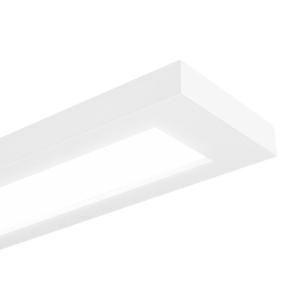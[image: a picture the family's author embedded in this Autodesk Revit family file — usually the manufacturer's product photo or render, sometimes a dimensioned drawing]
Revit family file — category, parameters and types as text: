
# Revit family: 3f_filippi_-_3f_travetta_op_3f_filippi_-_10731_-_3f_travetta_led_1x18w_op_l1290
name_source: partatom
category: Lighting Fixtures
units: mm (PartAtom-declared; Revit-internal decimal feet)

## family parameters
Cut with Voids When Loaded = No
Host = Face
Light Source = No
Part Type = Normal
Room Calculation Point = No
Round Connector Dimension = Use Diameter
Shared = No

## types (1)
- 3F Filippi - 3F Travetta OP (1 x LED, 2265 lm, 20 W, 4000 K)
    Apparent Load = 20 VA
    Approval mark = ENEC
    CIE Flux Codes = 49 81 97 100 100
    Color Rendering = 80
    Color Temperature = 4000 K
    Control Gear = Electronic ballast
    Default Elevation = 1800 mm
    Description = ILLUMINOTECHNICAL
Luminous efficiency 100% (DLOR 100%, ULOR 0%).
Initial luminous flux of the luminaire 2265 lm.
Direct symmetric distribution.
Installation Interdistance Transv.D = 1.20 x hu - Long.D = 1.20 x hu.
Tabular UGR (CIE 117 - 4H-8H; S=0.25H; 70/50/20): RUG 20.9 - 21.7.
Beam angle: 105° - 107°.
Luminous efficacy 113 lm/W.
Lifetime (L93/B10): 30000 h. (tq+25°C)
Lifetime (L90/B10): 50000 h. (tq+25°C)
Lifetime (L85/B10): 80000 h. (tq+25°C)
Lifetime (L80/B10): 100000 h. (tq+25°C)
Sudden decreased luminous flux after 50000 hours: 0% (C0).
Photobiological safety in compliance with IEC/TR 62778: RG0 risk exempt, (IEC 62471).
In compliance with IEC/EN 62722-2-1 - IEC/EN 62717 standards.

SOURCE
Linear LED module 18W/840.
Energy efficiency class (UE 2019/2020 - UE 2019/2015): D.
CIE 13.3 Colour rendering index: CRI >80 (R9 <50%).
IES TM-30 Fidelity Index: Rf = 84 Rg = 95.
CCT nominal colour temperature 4000 K.
Colour initial tolerance (MacAdam): SDCM 2.

MECHANICAL
Housing with squared shape in white painted galvannealed steel, with nonreflecting surface.
Flow recuperator in semi-glossy aluminium.
Opal methacrylate (PMMA) flat diffuser, anti-glare.
Luminaire with limited surface temperature. - D - (EN 60598-2-24)
Dimensions: 1290x190 mm, height 60 mm. Weight 4.165 kg.
IP20 protection degree.
Glow-wire test resistance 650°C.

ELECTRICAL
Halogen Free electronic wiring 230V-50/60Hz, power factor 0.90, THD <25%, constant output current, SELV, class I, 1 driver.
Power of the luminaire 20 W.
CE - IEC 60598-1 - EN 60598-1.
SAFE FLICKER: PstLM=<1 and SVM=<0.4 (IEC TR 61547-1 and IEC TR 63158), to ensure a more comfortable and safe light.
Luminaire compliant with EN 60598-2-22 for power supply from a centralised emergency system CPSS (Central Power Supply System), not incorporated in the luminaire - high risk areas excluded. The default power and flux are 100% in AC and 100% in DC.
Ambient temperature from 0°C to +25°C.
Temperature class T6 max 85°C.
5-pole terminal block for cascade line connection with connection capacity 2x2.5 mm².
Relative humidity UR: <85%.

INSTALLATION
Ceiling / Suspended.
All accessories dedicated to this product are available on the Catalog and on our website www.3F-Filippi.com.

APPLICATIONS
In environments, even with reduced height, requiring a comfortable light.
Exhibitions area, halls, great halls and shops.

WARNING
Luminaire designed for disposal/recycling at end-of-life.
Replaceable (LED only) light source by a professional. Replaceable control gear by a professional.
    Height = 60 mm  [stored 0.19685 ft]
    Lamp = 1 x LED
    Lamp Light Flux = 2265 lm
    Lamp Power = 20 W
    Lamp count = 1
    Length = 1290 mm
    Lifetime = 50000 h
    Luminous efficacy = 113 lm/W
    Manufacturer = 3F Filippi
    ModVariant = No
    Model = 3F Filippi - 10731 - 3F Travetta LED 1x18W OP L1290
    Mounting Place = Ceiling
    Mounting Type = Pendant
    Number of Poles = 1
    OnlyDefault = Yes
    Power Factor = 1
    Product Name = 3F Filippi - 3F Travetta OP
    Product group = pendant luminaire
    ProductGroupID = 9
    Protection Class = Protection class I
    Protection Degree = IP 20
    RLX_Detail_Level = 1
    RLX_Emergency_Light_Flux = 0 lm
    RLX_Emergency_Type = 0
    RLX_Emergency_Type_DB = No
    RlxData = <blob elided: 31189 chars, md5=3942ae12>
    Socket = socket
    Standby Power = 0 W
    System Light Flux = 2265 lm
    System Power = 20 W
    Type Comments = Product without accessories
    Type Image = 3ffilippi_3f_travetta_led_op.jpg
    URL = http://relux.com
    VarID = ---
    Voltage = 0 V
    Weight = 0.00 kg
    Width = 190 mm  [stored 0.62336 ft]

note: [stored X ft] marks values corroborated as IEEE doubles in the binary element streams (Revit-internal decimal feet)

## geometry (parser evidence)
native form markers: Blend x4, Sweep x9
no freeform markers — native parametric forms only
